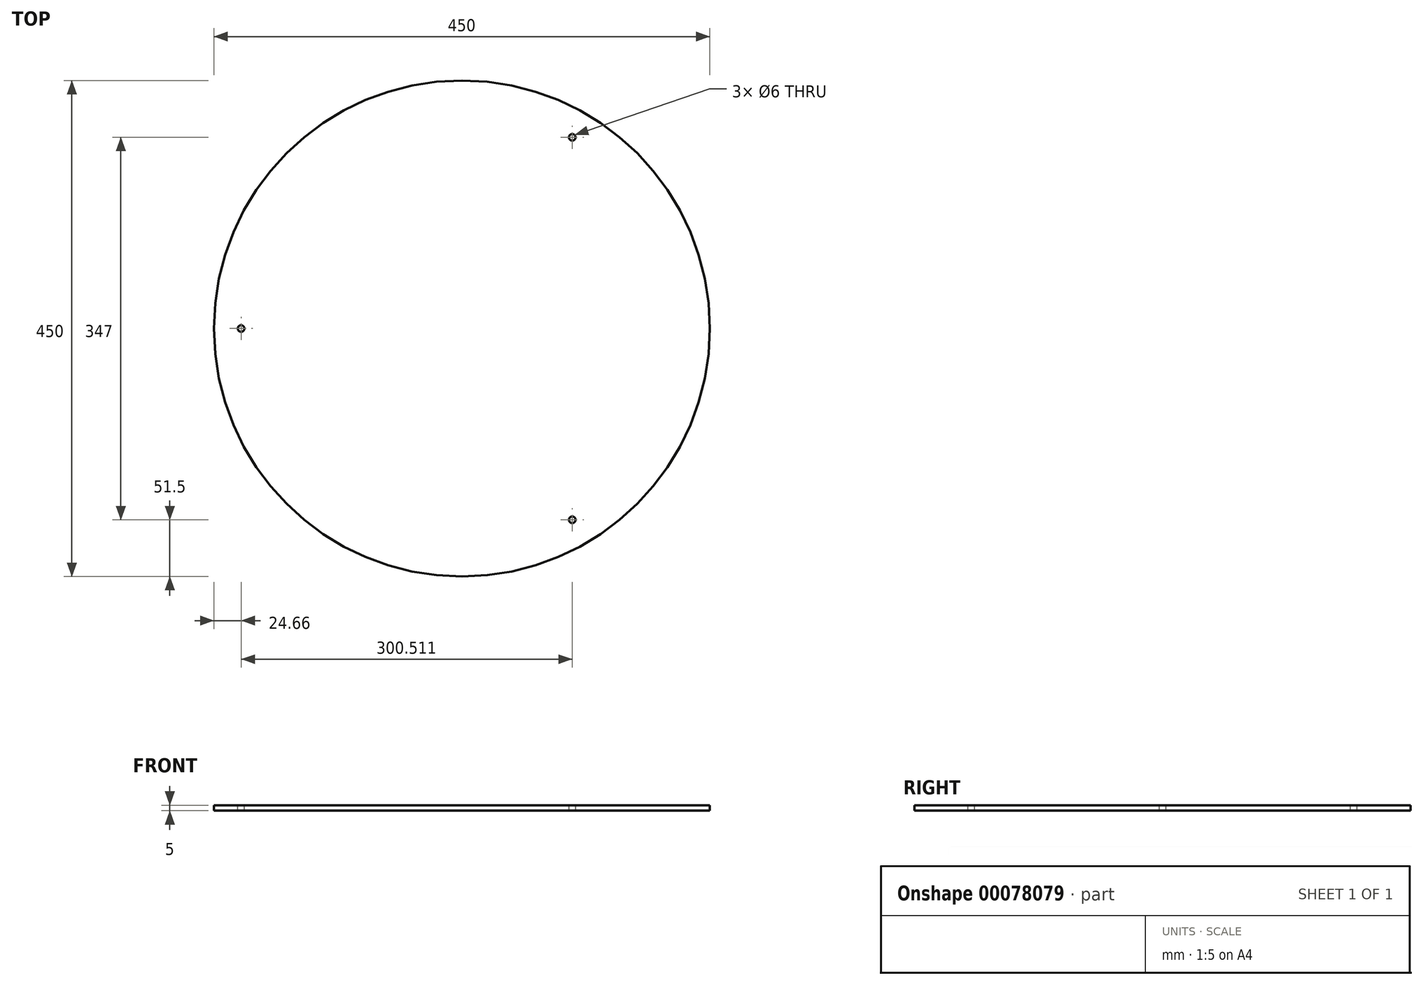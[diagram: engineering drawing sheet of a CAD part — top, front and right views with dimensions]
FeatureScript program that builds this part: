
annotation { "Feature Type Name" : "Feature", "Feature Type Description" : "" }
export const myFeature = defineFeature(function(context is Context, id is Id, definition is map)
    precondition{}
    {
        {
            var Q0;
            Q0=qCreatedBy(makeId("Top.planeOp"),FACE);
            var sketch = newSketch(context, id + "F0", { "sketchPlane" : qUnion([Q0])});
            skCircle(sketch, "E0.cCircle", {"center": v(0, 0) * mm, "radius": 100.17 * mm, "construction": true});
            skLineSegment(sketch, "E0.0", {"start": v(100.17, 173.5) * mm, "end": v(100.17, -173.5) * mm});
            skLineSegment(sketch, "E0.1", {"start": v(100.17, -173.5) * mm, "end": v(-200.34, 0) * mm});
            skLineSegment(sketch, "E0.2", {"start": v(-200.34, 0) * mm, "end": v(100.17, 173.5) * mm});
            skPoint(sketch, "E0.0.midPoint", {"position": v(100.17, 0) * mm});
            skCircle(sketch, "E1", {"center": v(0, 0) * mm, "radius": 225 * mm});
            skSolve(sketch);
        }
        {
            var Q0;
            Q0 = qSketchRegion(id + "F0", true);
            var Q1;
            Q1=makeQuery(id+"F0.imprint","IMPRINT",FACE,{"disambiguationData":[TD([[makeQuery(id+"F0.imprint","IMPRINT",EDGE,{"derivedFrom":sQuery(id+"F0.wireOp",EDGE,"E0.0")}),-1.0]])]});
            extrude(context, id + "F1", {"entities" : qUnion([Q0, Q1]), "depth" : 5 * mm, "offsetDistance" : 25 * mm});
        }
        {
            var Q0;
            Q0=sQuery(id+"F0.wireOp",VERTEX,"E0.0.start");
            var Q1;
            Q1=sQuery(id+"F0.wireOp",VERTEX,"E0.1.end");
            var Q2;
            Q2=sQuery(id+"F0.wireOp",VERTEX,"E0.0.end");
            var Q3;
            Q3=makeQuery(id+"F1.opExtrude","SWEPT_BODY",BODY,{"disambiguationData":[OSD([sQuery(id+"F0.wireOp",EDGE,"E1")])]});
            hole(context, id + "F2", {"style" : HoleStyle.SIMPLE, "endStyle" : HoleEndStyle.THROUGH, "oppositeDirection" : true, "holeDiameter" : 6 * mm, "majorDiameter" : 5 * mm, "tappedDepth" : 12 * mm, "tapClearance" : 3, "locations" : qUnion([Q0, Q1, Q2]), "scope" : qUnion([Q3])});
        }
    });
